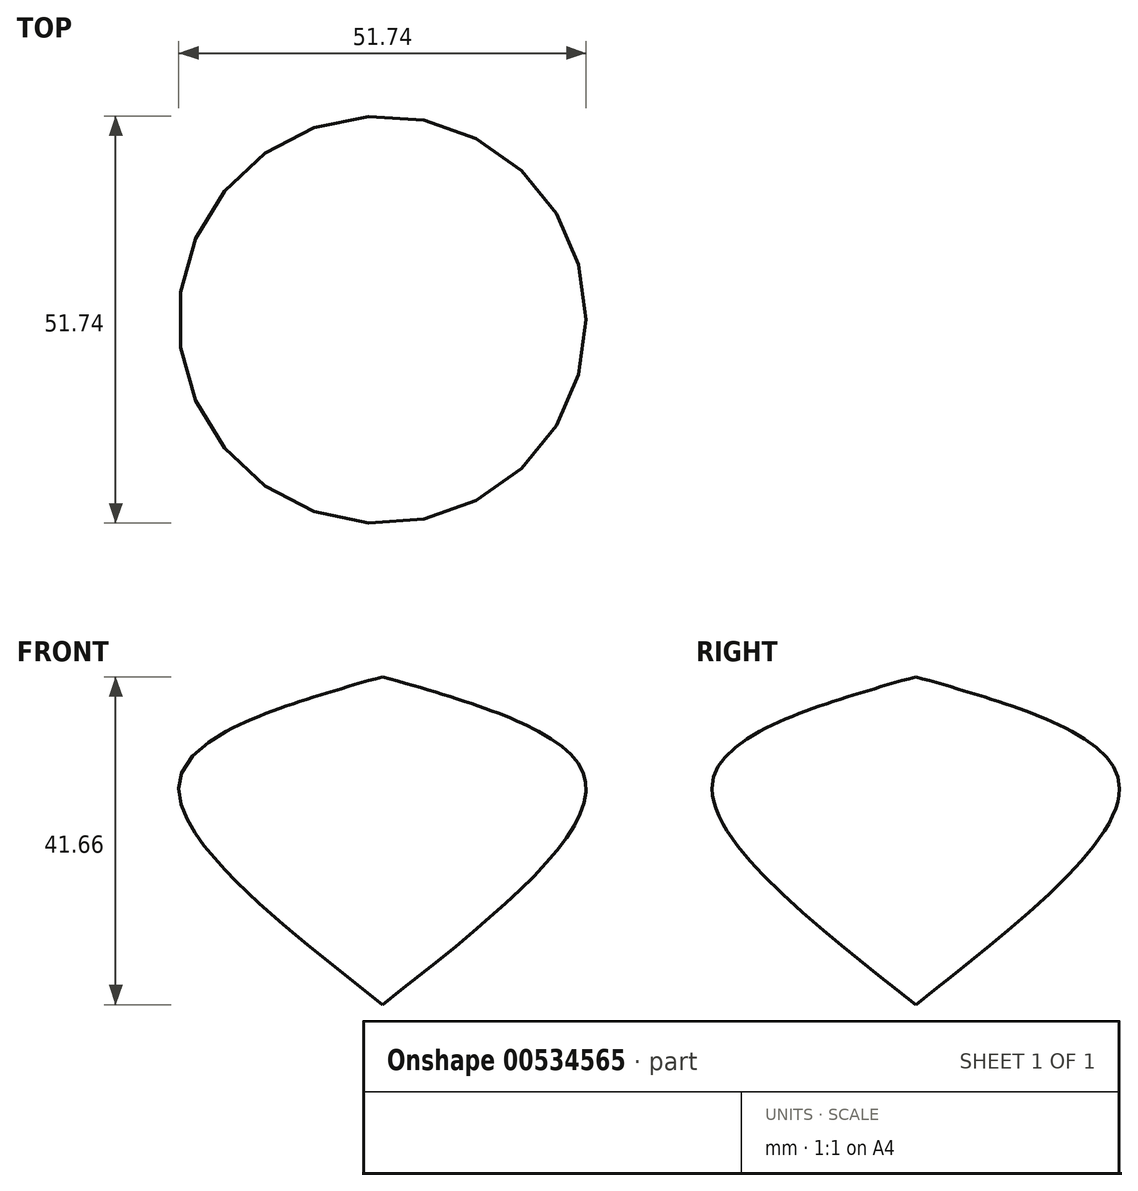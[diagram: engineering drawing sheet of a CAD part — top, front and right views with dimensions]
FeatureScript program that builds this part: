
annotation { "Feature Type Name" : "Feature", "Feature Type Description" : "" }
export const myFeature = defineFeature(function(context is Context, id is Id, definition is map)
    precondition{}
    {
        {
            var Q0;
            Q0=qCreatedBy(makeId("Front.planeOp"),FACE);
            var sketch = newSketch(context, id + "F0", { "sketchPlane" : qUnion([Q0])});
            skLineSegment(sketch, "E0", {"start": v(0, 0) * mm, "end": v(0, 41.66) * mm});
            skFitSpline(sketch, "E1", {"points": [v(0, 0) * mm, v(25.79, 28.43) * mm, v(0, 41.66) * mm], "startDerivative": vector(75.93, 59.75) * mm, "endDerivative": vector(-79.57, 22.7) * mm});
            skCircle(sketch, "E2", {"center": v(0, 41.66) * mm, "radius": 21.03 * mm});
            skSolve(sketch);
        }
        {
            var Q0;
            Q0=makeQuery(id+"F0.imprint","IMPRINT",FACE,{"disambiguationData":[TD([[makeQuery(id+"F0.imprint","IMPRINT",EDGE,{"derivedFrom":sQuery(id+"F0.wireOp",EDGE,"E0")}),-1.0]])]});
            var Q1;
            Q1=sQuery(id+"F0.wireOp",EDGE,"E0");
            revolve(context, id + "F1", {"entities" : qUnion([Q0]), "axis" : qUnion([Q1]), "revolveType" : RevolveType.FULL});
        }
        {
            var Q0;
            Q0=sQuery(id+"F0.wireOp",EDGE,"E2");
            extrude(context, id + "F2", {"bodyType" : ToolBodyType.SURFACE, "surfaceEntities" : qUnion([Q0]), "depth" : 127 * mm, "offsetDistance" : 25.4 * mm});
        }
    });
